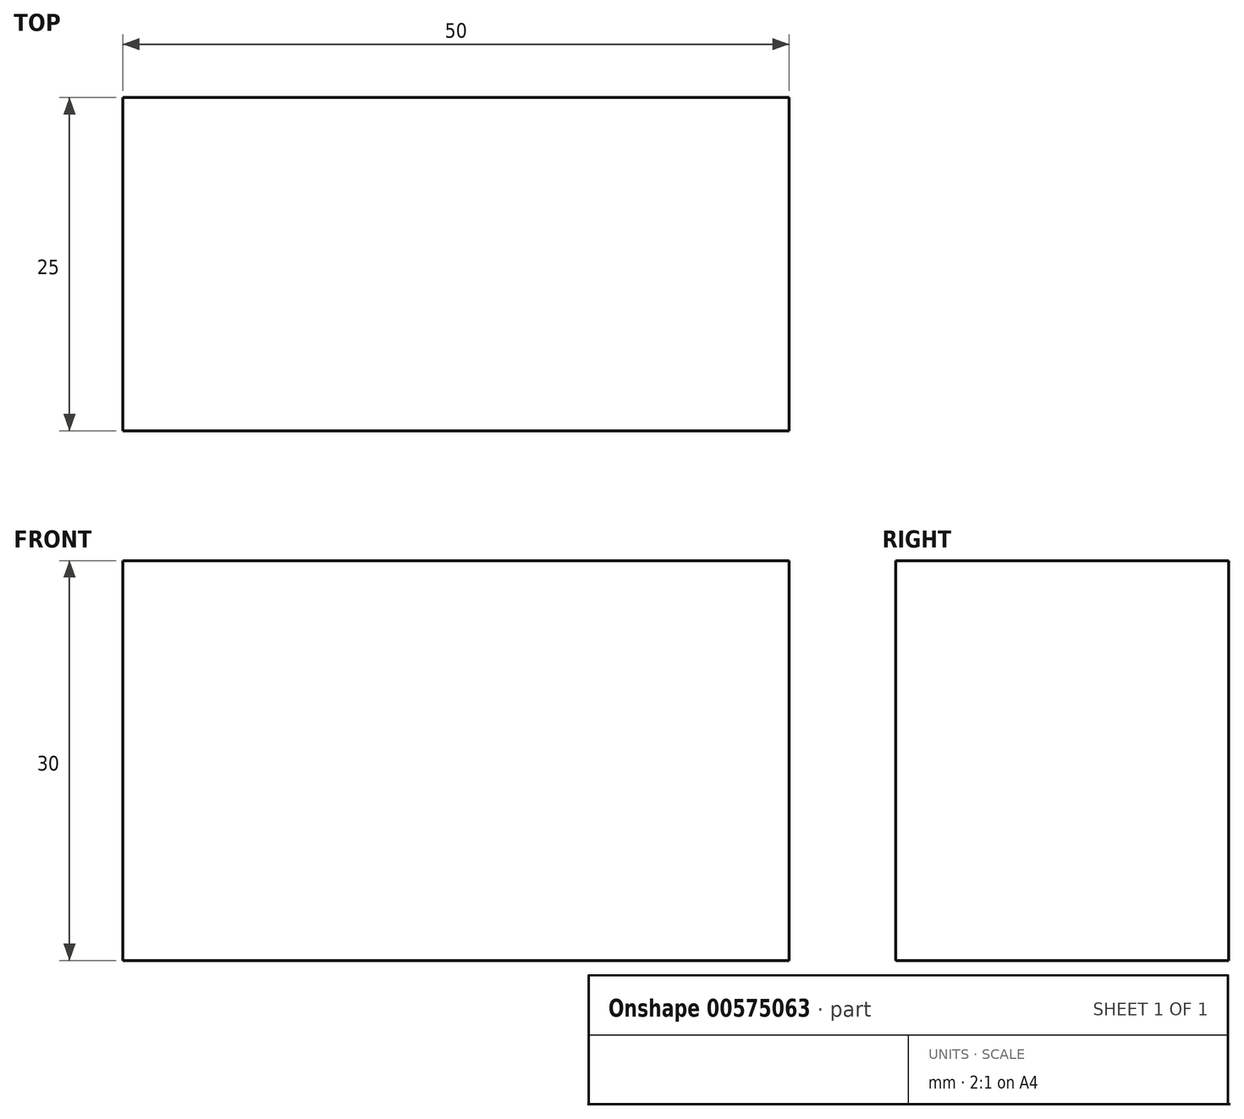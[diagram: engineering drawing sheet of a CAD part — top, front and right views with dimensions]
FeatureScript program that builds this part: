
annotation { "Feature Type Name" : "Feature", "Feature Type Description" : "" }
export const myFeature = defineFeature(function(context is Context, id is Id, definition is map)
    precondition{}
    {
        {
            var Q0;
            Q0=qCreatedBy(makeId("Front.planeOp"),FACE);
            var sketch = newSketch(context, id + "F0", { "sketchPlane" : qUnion([Q0])});
            skLineSegment(sketch, "E0.bottom", {"start": v(25, 15) * mm, "end": v(-25, 15) * mm});
            skLineSegment(sketch, "E0.top", {"start": v(25, -15) * mm, "end": v(-25, -15) * mm});
            skLineSegment(sketch, "E0.left", {"start": v(25, 15) * mm, "end": v(25, -15) * mm});
            skLineSegment(sketch, "E0.right", {"start": v(-25, 15) * mm, "end": v(-25, -15) * mm});
            skPoint(sketch, "E0.middle", {"position": v(0, 0) * mm});
            skSolve(sketch);
        }
        {
            var Q0;
            Q0 = qSketchRegion(id + "F0", true);
            extrude(context, id + "F1", {"entities" : qUnion([Q0]), "endBound" : BoundingType.SYMMETRIC, "depth" : 25 * mm, "offsetDistance" : 25 * mm});
        }
    });
